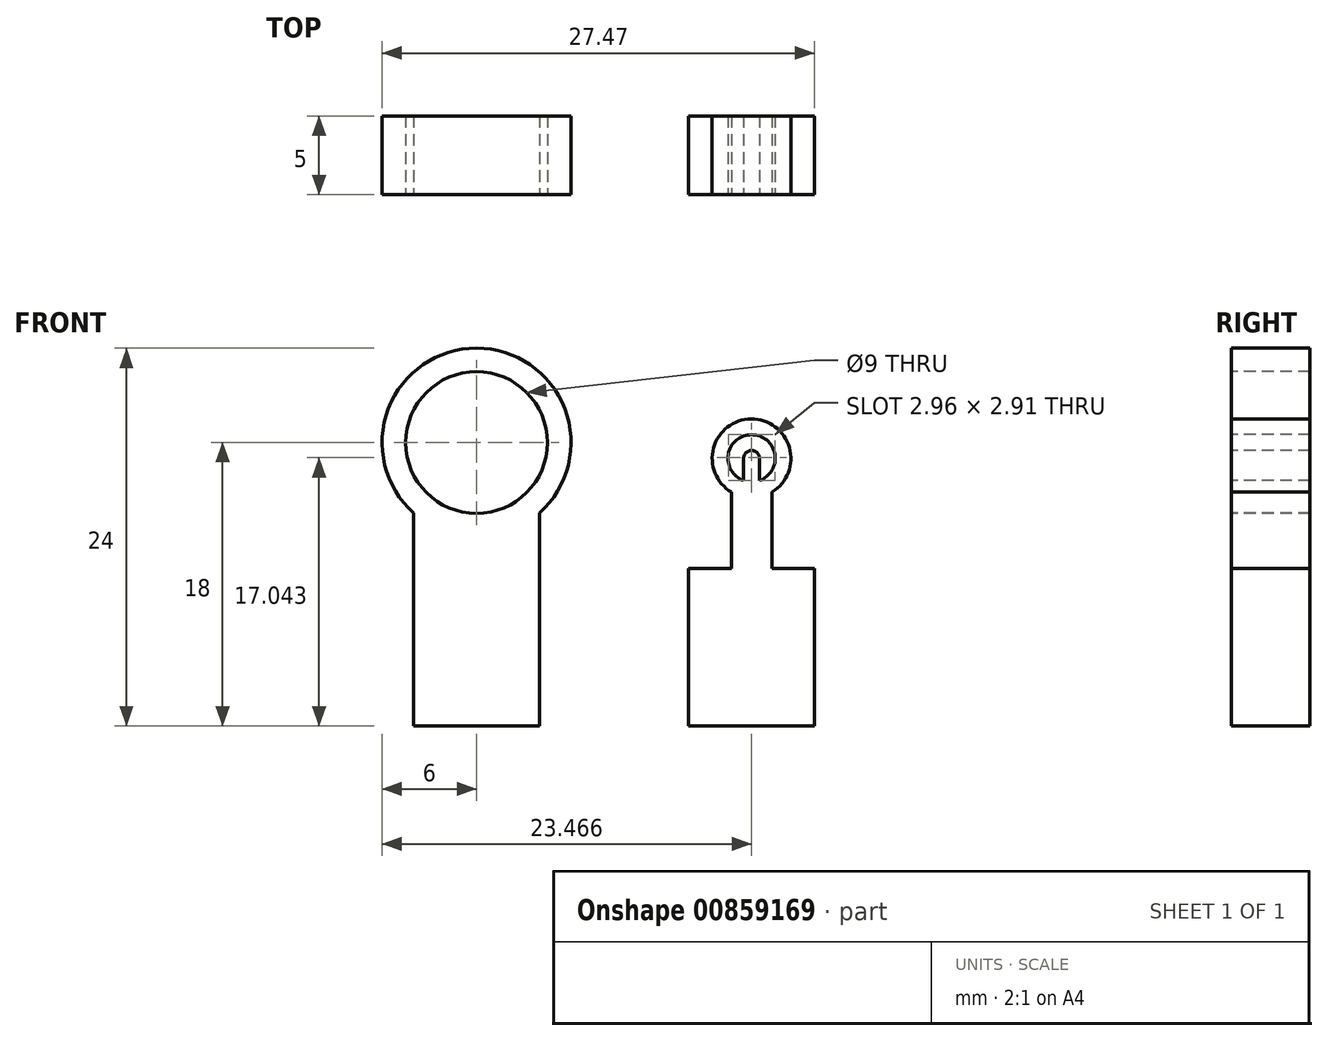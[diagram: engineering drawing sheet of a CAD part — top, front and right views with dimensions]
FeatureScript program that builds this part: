
annotation { "Feature Type Name" : "Feature", "Feature Type Description" : "" }
export const myFeature = defineFeature(function(context is Context, id is Id, definition is map)
    precondition{}
    {
        {
            var Q0;
            Q0=qCreatedBy(makeId("Front.planeOp"),FACE);
            var sketch = newSketch(context, id + "F0", { "sketchPlane" : qUnion([Q0])});
            skLineSegment(sketch, "E0.bottom", {"start": v(0, 0) * mm, "end": v(-4, 0) * mm});
            skLineSegment(sketch, "E0.top", {"start": v(0, 12) * mm, "end": v(-4, 12) * mm});
            skLineSegment(sketch, "E0.left", {"start": v(0, 0) * mm, "end": v(0, 12) * mm});
            skLineSegment(sketch, "E0.right", {"start": v(-4, 0) * mm, "end": v(-4, 12) * mm});
            skLineSegment(sketch, "E1.bottom", {"start": v(0, 0) * mm, "end": v(4, 0) * mm});
            skLineSegment(sketch, "E1.top", {"start": v(0, 12) * mm, "end": v(4, 12) * mm});
            skLineSegment(sketch, "E1.right", {"start": v(4, 0) * mm, "end": v(4, 12) * mm});
            skLineSegment(sketch, "E2", {"start": v(0, 12) * mm, "end": v(0, 24) * mm});
            skCircle(sketch, "E3", {"center": v(0, 18) * mm, "radius": 6 * mm});
            skCircle(sketch, "E4", {"center": v(0, 18) * mm, "radius": 4.5 * mm});
            skLineSegment(sketch, "E5", {"start": v(-4, 12) * mm, "end": v(-4, 13.53) * mm});
            skLineSegment(sketch, "E6", {"start": v(4, 12) * mm, "end": v(4, 13.53) * mm});
            skSolve(sketch);
        }
        {
            var Q0;
            Q0 = qSketchRegion(id + "F0", true);
            extrude(context, id + "F1", {"entities" : qUnion([Q0]), "depth" : -5 * mm, "offsetDistance" : 25 * mm});
        }
        {
            var Q0;
            Q0=qCreatedBy(makeId("Front.planeOp"),FACE);
            var sketch = newSketch(context, id + "F2", { "sketchPlane" : qUnion([Q0])});
            skLineSegment(sketch, "E7.bottom", {"start": v(13.47, 0) * mm, "end": v(21.47, 0) * mm});
            skLineSegment(sketch, "E7.top", {"start": v(13.47, 10) * mm, "end": v(21.47, 10) * mm});
            skLineSegment(sketch, "E7.left", {"start": v(13.47, 0) * mm, "end": v(13.47, 10) * mm});
            skLineSegment(sketch, "E7.right", {"start": v(21.47, 0) * mm, "end": v(21.47, 10) * mm});
            skLineSegment(sketch, "E8.bottom", {"start": v(17.47, 10) * mm, "end": v(16.47, 10) * mm});
            skLineSegment(sketch, "E9.bottom", {"start": v(17.47, 10) * mm, "end": v(18.47, 10) * mm});
            skLineSegment(sketch, "E10", {"start": v(17.47, 10) * mm, "end": v(17.47, 24) * mm});
            skCircle(sketch, "E11", {"center": v(17.47, 17) * mm, "radius": 1.5 * mm});
            skCircle(sketch, "E12", {"center": v(17.47, 17) * mm, "radius": 2.5 * mm});
            skLineSegment(sketch, "E13.bottom", {"start": v(17.47, 10) * mm, "end": v(16.2, 10) * mm});
            skLineSegment(sketch, "E13.top", {"start": v(17.47, 14.85) * mm, "end": v(16.2, 14.85) * mm});
            skLineSegment(sketch, "E13.left", {"start": v(17.47, 10) * mm, "end": v(17.47, 14.85) * mm});
            skLineSegment(sketch, "E13.right", {"start": v(16.2, 10) * mm, "end": v(16.2, 14.85) * mm});
            skLineSegment(sketch, "E14.bottom", {"start": v(17.47, 10) * mm, "end": v(18.77, 10) * mm});
            skLineSegment(sketch, "E14.top", {"start": v(17.47, 14.87) * mm, "end": v(18.77, 14.87) * mm});
            skLineSegment(sketch, "E14.left", {"start": v(17.47, 10) * mm, "end": v(17.47, 14.87) * mm});
            skLineSegment(sketch, "E14.right", {"start": v(18.77, 10) * mm, "end": v(18.77, 14.87) * mm});
            skLineSegment(sketch, "E15.bottom", {"start": v(17.47, 15.5) * mm, "end": v(17.97, 15.5) * mm});
            skLineSegment(sketch, "E15.top", {"start": v(17.47, 16.5) * mm, "end": v(17.97, 16.5) * mm});
            skLineSegment(sketch, "E15.left", {"start": v(17.47, 15.5) * mm, "end": v(17.47, 16.5) * mm});
            skLineSegment(sketch, "E15.right", {"start": v(17.97, 15.5) * mm, "end": v(17.97, 16.5) * mm});
            skLineSegment(sketch, "E16.bottom", {"start": v(17.47, 15.5) * mm, "end": v(16.97, 15.5) * mm});
            skLineSegment(sketch, "E16.top", {"start": v(17.47, 16.5) * mm, "end": v(16.97, 16.5) * mm});
            skLineSegment(sketch, "E16.right", {"start": v(16.97, 15.5) * mm, "end": v(16.97, 16.5) * mm});
            skCircle(sketch, "E17", {"center": v(17.47, 17) * mm, "radius": 0.5 * mm});
            skLineSegment(sketch, "E18", {"start": v(17.97, 16.5) * mm, "end": v(17.97, 17) * mm});
            skLineSegment(sketch, "E19", {"start": v(16.97, 16.5) * mm, "end": v(16.97, 17) * mm});
            skSolve(sketch);
        }
        {
            var Q0;
            {var subQ4=sQuery(id+"F2.wireOp",EDGE,"E15.top");Q0=makeQuery(id+"F2.imprint","IMPRINT",FACE,{"disambiguationData":[TD([[makeQuery(id+"F2.imprint","IMPRINT",EDGE,{"derivedFrom":subQ4}),-1.0]])]});}
            var Q1;
            {var subQ4=sQuery(id+"F2.wireOp",EDGE,"E16.top");Q1=makeQuery(id+"F2.imprint","IMPRINT",FACE,{"disambiguationData":[TD([[makeQuery(id+"F2.imprint","IMPRINT",EDGE,{"derivedFrom":subQ4}),1.0]])]});}
            var Q2;
            {var subQ0=sQuery(id+"F2.wireOp",EDGE,"E16.bottom");Q2=makeQuery(id+"F2.imprint","IMPRINT",FACE,{"disambiguationData":[TD([[makeQuery(id+"F2.imprint","IMPRINT",EDGE,{"derivedFrom":subQ0}),-1.0]])]});}
            var Q3;
            {var subQ0=sQuery(id+"F2.wireOp",EDGE,"E15.bottom");Q3=makeQuery(id+"F2.imprint","IMPRINT",FACE,{"disambiguationData":[TD([[makeQuery(id+"F2.imprint","IMPRINT",EDGE,{"derivedFrom":subQ0}),1.0]])]});}
            var Q4;
            {var subQ0=sQuery(id+"F2.wireOp",EDGE,"E15.top");Q4=makeQuery(id+"F2.imprint","IMPRINT",FACE,{"disambiguationData":[TD([[makeQuery(id+"F2.imprint","IMPRINT",EDGE,{"derivedFrom":subQ0}),1.0]])]});}
            var Q5;
            {var subQ0=sQuery(id+"F2.wireOp",EDGE,"E17");var subQ4=makeQuery(id+"F2.imprint","INTERSECT",VERTEX,{"derivedFrom":[subQ0,sQuery(id+"F2.wireOp",EDGE,"E18")]});Q5=makeQuery(id+"F2.imprint","IMPRINT",FACE,{"disambiguationData":[TD([[makeQuery(id+"F2.imprint","IMPRINT",EDGE,{"disambiguationData":[TD([[subQ4,-1.0]])],"derivedFrom":subQ0}),1.0]])]});}
            var Q6;
            {var subQ0=sQuery(id+"F2.wireOp",EDGE,"E17");var subQ4=makeQuery(id+"F2.imprint","INTERSECT",VERTEX,{"derivedFrom":[subQ0,sQuery(id+"F2.wireOp",EDGE,"E19")]});Q6=makeQuery(id+"F2.imprint","IMPRINT",FACE,{"disambiguationData":[TD([[makeQuery(id+"F2.imprint","IMPRINT",EDGE,{"disambiguationData":[TD([[subQ4,1.0]])],"derivedFrom":subQ0}),1.0]])]});}
            var Q7;
            {var subQ0=sQuery(id+"F2.wireOp",EDGE,"E16.top");Q7=makeQuery(id+"F2.imprint","IMPRINT",FACE,{"disambiguationData":[TD([[makeQuery(id+"F2.imprint","IMPRINT",EDGE,{"derivedFrom":subQ0}),-1.0]])]});}
            var Q8;
            {var subQ5=sQuery(id+"F2.wireOp",EDGE,"E13.top");Q8=makeQuery(id+"F2.imprint","IMPRINT",FACE,{"disambiguationData":[TD([[makeQuery(id+"F2.imprint","IMPRINT",EDGE,{"derivedFrom":subQ5}),-1.0]])]});}
            var Q9;
            {var subQ0=sQuery(id+"F2.wireOp",EDGE,"E14.top");Q9=makeQuery(id+"F2.imprint","IMPRINT",FACE,{"disambiguationData":[TD([[makeQuery(id+"F2.imprint","IMPRINT",EDGE,{"derivedFrom":subQ0}),1.0]])]});}
            var Q10;
            {var subQ0=sQuery(id+"F2.wireOp",EDGE,"E14.top");Q10=makeQuery(id+"F2.imprint","IMPRINT",FACE,{"disambiguationData":[TD([[makeQuery(id+"F2.imprint","IMPRINT",EDGE,{"derivedFrom":subQ0}),-1.0]])]});}
            var Q11;
            {var subQ0=sQuery(id+"F2.wireOp",EDGE,"E13.top");Q11=makeQuery(id+"F2.imprint","IMPRINT",FACE,{"disambiguationData":[TD([[makeQuery(id+"F2.imprint","IMPRINT",EDGE,{"derivedFrom":subQ0}),1.0]])]});}
            var Q12;
            {var subQ5=sQuery(id+"F2.wireOp",EDGE,"E14.right");Q12=makeQuery(id+"F2.imprint","IMPRINT",FACE,{"disambiguationData":[TD([[makeQuery(id+"F2.imprint","IMPRINT",EDGE,{"derivedFrom":subQ5}),1.0]])]});}
            var Q13;
            {var subQ0=sQuery(id+"F2.wireOp",EDGE,"E13.right");Q13=makeQuery(id+"F2.imprint","IMPRINT",FACE,{"disambiguationData":[TD([[makeQuery(id+"F2.imprint","IMPRINT",EDGE,{"derivedFrom":subQ0}),-1.0]])]});}
            var Q14;
            Q14=makeQuery(id+"F2.imprint","IMPRINT",FACE,{"disambiguationData":[TD([[makeQuery(id+"F2.imprint","IMPRINT",EDGE,{"derivedFrom":sQuery(id+"F2.wireOp",EDGE,"E7.bottom")}),1.0]])]});
            extrude(context, id + "F3", {"entities" : qUnion([Q0, Q1, Q2, Q3, Q4, Q5, Q6, Q7, Q8, Q9, Q10, Q11, Q12, Q13, Q14]), "depth" : -5 * mm, "offsetDistance" : 25 * mm});
        }
    });
